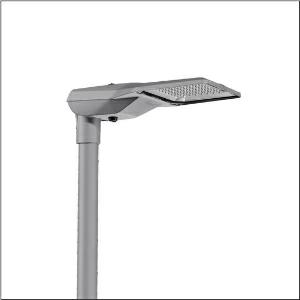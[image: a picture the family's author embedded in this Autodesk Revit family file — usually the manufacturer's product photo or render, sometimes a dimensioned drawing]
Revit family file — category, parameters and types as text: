
# Revit family: streetlight_sl_21_iq_midi___st0_5a_5xe3b31y08mb_2f18
name_source: partatom
category: Lighting Fixtures
units: mm (PartAtom-declared; Revit-internal decimal feet)

## family parameters
Cut with Voids When Loaded = No
Host = Face
Light Source = No
Part Type = Normal
Room Calculation Point = No
Round Connector Dimension = Use Diameter
Shared = No

## types (1)
- --- (1 x LED, 18340 lm, 129.3 W, 3000K)
    Apparent Load = 129 VA
    CIE Flux Codes = 41 75 97 100 100
    Color Rendering = 70
    Color Temperature = 3000K
    Default Elevation = 1800 mm
    Description = Streetlight SL 21 iQ midi, mast luminaire, primary light control with lens, of PMMA, primary optical cover: cover, of toughened safety glass, transparent, light distribution: ST0.5a, light emission: direct distribution, primary light characteristic: asymmetric, installation type: post-top, side-entry, LED, High Power LED, rated luminous flux: 18.340lm, luminous efficacy: 142lm/W, light colour: 730, colour temperature: 3000K, control: presetting dimming logarithmic, Street-Remote, Auto-Match, Temp-Guard, Lumen-Switch, Night-Set, Smart-Wire, Light-Fading, Desk-Remote (wireless, voltage-free reading and setting of iQ features in the workshop via application-optimized NFC function/RFID function), optimised constant luminous flux control (CLO 2.0), mains connection: 230..240V, AC, 50/60Hz, start of lifetime: 129W, end of service life: 142W, reduction: 56W, luminaire housing, of diecast aluminium, powder-coated, Siteco® metallic grey (DB 702S), corrosivity category C5 mid according to DIN EN ISO 12944, please order mast flange separately, inclination adjustable: 0°, 5°, 10°, 15°, sealing non-destructively replaceable, multi-level sealing system, length: 644mm, width: 335mm, height: 110mm, mast flange for spigot size: 42mm (side-entry): 5XC10008XM4, 60/48mm (side-entry/post-top): 5XC10108XM2, 76/60mm (side-entry/post-top): 5XC10108XM1, Smart Interface below and above, protection rating (complete): IP66, insulation class (complete): insulation class II (safety insulation), certification: CE, ENEC, ENEC+, VDE, impact resistance: IK09, permissible operating ambient temperature for outdoor applications: -40..+50°C, standard-compliant lighting for roads and squares, packaging unit: 1 piece

Light Distribution: ST0.5a
    Height = 111 mm
    Lamp = 1 x LED
    Lamp Light Flux = 18340 lm
    Lamp Power = 129.3 W
    Lamp count = 1
    Length = 644 mm
    Luminous efficacy = 142 lm/W
    Manufacturer = Siteco
    ModVariant = No
    Model = 5XE3B31Y08MB
    Number of Poles = 1
    OnlyDefault = Yes
    Power Factor = 1
    Product Name = Streetlight SL 21 iQ midi | ST0.5a
    Product group = mast luminaire | pylon top
    ProductGroupID = 6100
    Protection Class = Protection class II
    Protection Degree = IP 66
    RLX_Detail_Level = 1
    RLX_Emergency_Light_Flux = 0 lm
    RLX_Emergency_Type = 0
    RLX_Emergency_Type_DB = No
    RlxData = <blob elided: 101877 chars, md5=0cf85e48>
    Socket = socket
    Standby Power = 0 W
    System Light Flux = 18340 lm
    System Power = 129 W
    Type Comments = factory setting: luminous flux: 100 % | dim-lin: 254 | 672 mA
    Type Image = l_1004304.jpg
    URL = http://relux.com
    VarID = @adj_046105
    Voltage = 0 V
    Weight = 0.00 kg
    Width = 336 mm

## geometry (parser evidence)
native form markers: Blend x4, Sweep x9
no freeform markers — native parametric forms only
